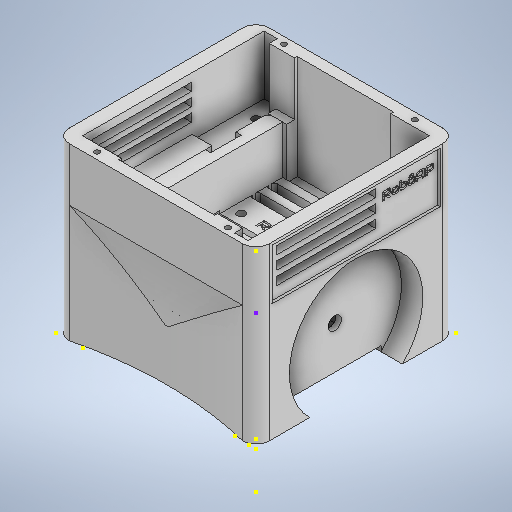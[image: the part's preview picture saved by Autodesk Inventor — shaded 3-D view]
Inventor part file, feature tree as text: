
AUTODESK INVENTOR PART (.ipt)
format: ipt  version: 2025.2 (Build 292293000, 293)  size: 1,790,464 bytes
history: native  units: mm
features: sketch x67, extrude x47, thread x13, other x8
ambient origin geometry x8: Origin, YZ Plane, XZ Plane, XY Plane, X Axis, Y Axis, Z Axis, Center Point
bodies: Body1 (feature_tree), Body2 (feature_tree)
feature tree (135):
  other  "CaseInterno.ipt"
  other  "Sólido1"
  extrude  "Extrusão1"  Depth=75.0mm
  sketch  "Esboço2"  dims[d15=26.0mm d16=0.0mm d18=26.0mm d19=0.0mm]
  extrude  "Extrusão2"  Depth=5.0mm
  extrude  "Extrusão3"  Depth=15.0mm TaperAngle=0.0deg
  extrude  "Extrusão4"  Depth=15.0mm TaperAngle=0.0deg
  sketch  "Esboço3"  dims[d20=65.0mm d21=0.0mm d22=26.0mm d23=0.0mm]
  sketch  "Esboço4"  dims[d26=26.0mm d27=0.0mm d28=65.0mm d29=0.0mm]
  extrude  "Extrusão5"  Depth=26.0mm TaperAngle=0.0deg
  extrude  "Extrusão6"  Depth=26.0mm TaperAngle=0.0deg
  sketch  "Esboço7"  dims[d36=8.0mm d37=0.0mm d38=10.0mm d39=0.0mm]
  extrude  "Extrusão7"  Depth=26.0mm TaperAngle=0.0deg
  extrude  "Extrusão8"  Depth=65.0mm TaperAngle=0.0deg
  extrude  "Extrusão9"  Depth=8.0mm TaperAngle=0.0deg
  sketch  "Esboço13"  dims[d47=9.0mm d48=90.0deg]
  sketch  "Esboço14"  dims[d49=55.0mm d50=0.0mm d51=5.0mm]
  extrude  "Extrusão11"  Depth=5.0mm
  extrude  "Extrusão12"  Depth=10.0mm TaperAngle=0.0deg
  extrude  "Extrusão13"  Depth=6.0mm
  extrude  "Extrusão14"  TaperAngle=180.0deg  [1 undecoded]
  sketch  "Esboço16"  dims[d55=3.0mm d56=55.0mm]
  extrude  "Extrusão15"  TaperAngle=90.0deg  [1 undecoded]
  extrude  "Extrusão16"  Depth=5.0mm
  sketch  "Esboço17"  dims[d57=3.0mm d58=13.0mm d59=0.0mm]
  extrude  "Extrusão17"  Depth=13.0mm TaperAngle=0.0deg
  extrude  "Extrusão18"  Depth=55.0mm
  sketch  "Esboço20"  dims[d67=3.0mm d68=0.0mm d69=4.0mm]
  extrude  "Extrusão19"  Depth=13.0mm TaperAngle=0.0deg
  extrude  "Extrusão20"  Depth=24.0mm
  sketch  "Esboço23"  dims[d79=10.0mm d80=0.0mm d81=10.0mm d82=0.0mm]
  extrude  "Extrusão21"  Depth=3.0mm TaperAngle=0.0deg
  extrude  "Extrusão22"  Depth=4.0mm
  sketch  "Esboço26"  dims[d90=65.0mm d91=20.0mm d92=0.0mm]
  extrude  "Extrusão23"  Depth=4.0mm
  extrude  "Extrusão24"  Depth=3.0mm
  thread  "Rosca1"  [1 undecoded]
  thread  "Rosca2"  [1 undecoded]
  thread  "Rosca3"  [1 undecoded]
  thread  "Rosca4"  [1 undecoded]
  extrude  "Extrusão25"  Depth=10.0mm TaperAngle=0.0deg
  sketch  "Esboço30"  dims[d100=39.0mm d101=0.0mm d102=2.0mm d103=0.0mm]
  extrude  "Extrusão26"  Depth=10.0mm TaperAngle=0.0deg
  sketch  "Esboço32"  dims[d112=5.0mm d113=5.0mm d114=5.0mm d115=5.0mm d116=5.0mm d117=44.0mm d118=0.0mm]
  extrude  "Extrusão27"  Depth=65.0mm
  sketch  "Esboço34"  dims[d121=3.0mm d122=3.0mm]
  extrude  "Extrusão28"  Depth=20.0mm TaperAngle=0.0deg
  sketch  "Esboço36"  dims[d127=11.0mm d128=0.0mm d129=11.0mm d130=0.0mm d131=11.0mm d132=0.0mm]
  sketch  "Esboço37"  dims[d133=8.0mm d134=2.5mm]
  sketch  "Esboço38"  dims[d135=8.0mm d136=2.5mm]
  extrude  "Extrusão29"  Depth=36.0mm
  extrude  "Extrusão30"  TaperAngle=90.0deg  [1 undecoded]
  extrude  "Extrusão31"  Depth=19.0mm TaperAngle=0.0deg
  sketch  "Esboço41"  dims[d141=2.0mm d142=2.0mm]
  extrude  "Extrusão32"  Depth=2.0mm TaperAngle=0.0deg
  extrude  "Extrusão33"  Depth=5.0mm
  thread  "Rosca5"  [1 undecoded]
  thread  "Rosca6"  [1 undecoded]
  thread  "Rosca7"  [1 undecoded]
  thread  "Rosca8"  [1 undecoded]
  extrude  "Extrusão34"  Depth=5.0mm
  thread  "Rosca9"  [1 undecoded]
  thread  "Rosca10"  [1 undecoded]
  thread  "Rosca11"  [1 undecoded]
  thread  "Rosca12"  [1 undecoded]
  extrude  "Extrusão35"  Depth=3.0mm
  extrude  "Extrusão36"  Depth=3.0mm
  sketch  "Esboço47"  dims[d173=16.0mm]
  sketch  "Esboço48"  dims[d177=44.0mm d178=0.0mm]
  sketch  "Esboço49"  dims[d179=10.0mm d180=0.0mm]
  sketch  "Esboço50"  dims[d181=11.0mm d182=0.0mm]
  sketch  "Esboço51"  dims[d183=28.0mm d184=0.0mm]
  sketch  "Esboço52"  dims[d189=5.0mm d190=0.0mm]
  sketch  "Esboço53"  dims[d193=2.0mm d194=0.0mm]
  extrude  "Extrusão37"  Depth=11.0mm TaperAngle=0.0deg
  extrude  "Extrusão38"  Depth=11.0mm TaperAngle=0.0deg
  thread  "Rosca13"  [1 undecoded]
  extrude  "Extrusão39"  Depth=2.5mm
  sketch  "Esboço56"  dims[d199=22.0mm d200=0.0mm]
  sketch  "Esboço58"  dims[d201=2.0mm d202=0.0mm]
  extrude  "Extrusão40"  Depth=2.5mm
  extrude  "Extrusão42"  Depth=8.0mm
  extrude  "Extrusão43"  Depth=2.0mm
  sketch  "Esboço60"  dims[d227=1.9mm]
  sketch  "Esboço61"  dims[d228=1.9mm]
  extrude  "Extrusão44"  Depth=2.0mm
  extrude  "Extrusão45"  Depth=11.0mm TaperAngle=0.0deg
  extrude  "Extrusão46"  Depth=11.0mm TaperAngle=0.0deg
  sketch  "Esboço65"  dims[d231=14.0mm d232=0.0mm]
  extrude  "Extrusão47"  Depth=1.0mm
  sketch  "Esboço69"  dims[d246=22.25mm d247=8.0mm d248=10.0mm]
  extrude  "Extrusão48"  Depth=1.0mm TaperAngle=0.0deg
  extrude  "Extrusão49"  Depth=2.5mm
  other  "Edição direta16"
  sketch  "Esboço1"  dims[d0=75.0mm d1=75.0mm]
  sketch  "Esboço5"  dims[d30=5.0mm d31=8.0mm d32=0.0mm]
  sketch  "Esboço6"  dims[d33=10.0mm d34=0.0mm d35=5.0mm]
  sketch  "Esboço8"  dims[d40=2.0mm d44=6.0mm]
  sketch  "Esboço9"  dims[d45=6.0mm d46=180.0deg]
  sketch  "Esboço15"  dims[d52=5.0mm d53=13.0mm d54=0.0mm]
  sketch  "Esboço18"  dims[d60=41.0mm d61=0.0mm d62=24.0mm]
  sketch  "Esboço19"  dims[d63=13.0mm d64=0.0mm d65=3.0mm d66=0.0mm]
  sketch  "Esboço21"  dims[d70=4.0mm d71=4.0mm]
  sketch  "Esboço22"  dims[d72=90.0deg d73=3.0mm d74=3.0mm d75=3.0mm d76=3.0mm d77=10.0mm d78=0.0mm]
  sketch  "Esboço24"  dims[d83=10.0mm d84=0.0mm d85=10.0mm d86=0.0mm]
  sketch  "Esboço25"  dims[d87=13.0mm d88=0.0mm d89=65.0mm]
  sketch  "Esboço27"  dims[d93=9.5mm d94=36.0mm]
  sketch  "Esboço28"  dims[d95=59.0mm d96=90.0deg]
  sketch  "Esboço29"  dims[d97=36.0mm d98=19.0mm d99=0.0mm]
  sketch  "Esboço31"  dims[d104=1.0mm d105=63.0mm d106=1.0mm d107=0.0mm d108=0.0mm d109=0.0mm d110=5.0mm d111=90.0deg]
  sketch  "Esboço33"  dims[d119=3.0mm d120=3.0mm]
  sketch  "Esboço35"  dims[d123=10.0mm d124=0.0mm d125=11.0mm d126=0.0mm]
  sketch  "Esboço39"  dims[d137=2.5mm d138=8.0mm]
  sketch  "Esboço40"  dims[d139=2.0mm d140=2.0mm]
  sketch  "Esboço42"  dims[d143=10.0mm d144=0.0mm d145=11.0mm d146=0.0mm]
  sketch  "Esboço43"  dims[d147=11.0mm d148=0.0mm d149=11.0mm d150=0.0mm]
  sketch  "Esboço44"  dims[d151=11.0mm d152=0.0mm d153=1.0mm]
  sketch  "Esboço45"  dims[d154=1.0mm d155=0.0mm d156=1.0mm d157=0.0mm]
  sketch  "Esboço46"  dims[d171=2.5mm d172=2.5mm]
  sketch  "Esboço54"  dims[d195=22.0mm d196=0.0mm]
  sketch  "Esboço55"  dims[d197=2.0mm d198=0.0mm]
  sketch  "Esboço59"  dims[d211=2.0mm d212=0.0mm]
  sketch  "Esboço62"  dims[d229=4.0mm d230=0.0mm]
  sketch  "Esboço68"  dims[d245=10.0mm]
  sketch  "Esboço70"  dims[d249=-0.25mm d250=0.0mm d251=0.0mm]
  sketch  "Esboço71"  dims[d24=0.5mm d25=0.872665mm d158=0.5mm d159=0.872665mm d160=0.5mm d161=0.872665mm d174=0.5mm d175=0.872665mm d176=0.5mm]
  other  "Sólido1::CaseInterno.ipt"
  other  "OperaçãoIdentificador9"
  sketch  "Esboço26_1"  dims[d2=5.0mm d3=5.0mm]
  sketch  "Esboço32_1"  dims[d4=3.0mm d5=0.0mm d6=15.0mm d7=0.0mm]
  sketch  "Esboço42_1"  dims[d8=3.0mm d9=0.0mm d10=15.0mm d11=0.0mm]
  sketch  "Esboço43_1"  dims[d12=50.0mm d13=26.0mm d14=0.0mm]
  other  "Sólido1_1"
  other  "Mover14"
  other  "Mover15"
note: 16 required parameter values undecoded (feature->parameter linkage not recoverable at this tier; creation-order binding heuristic only, values carry confidence <= 0.55)
